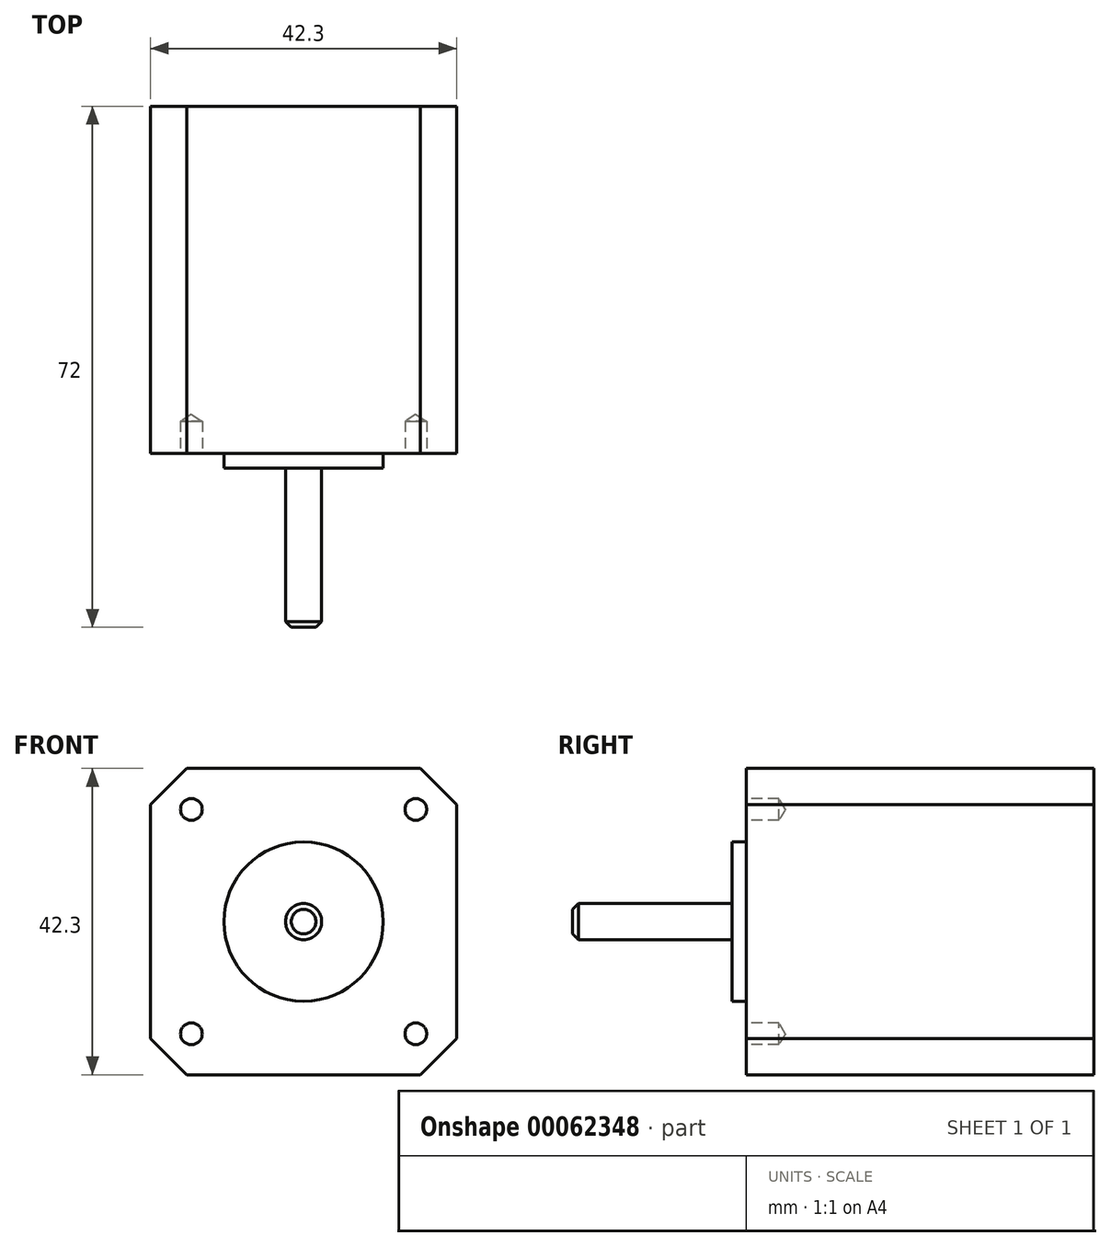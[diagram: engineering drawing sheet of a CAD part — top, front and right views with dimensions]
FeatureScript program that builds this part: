
annotation { "Feature Type Name" : "Feature", "Feature Type Description" : "" }
export const myFeature = defineFeature(function(context is Context, id is Id, definition is map)
    precondition{}
    {
        {
            var Q0;
            Q0=qCreatedBy(makeId("Front.planeOp"),FACE);
            var sketch = newSketch(context, id + "F0", { "sketchPlane" : qUnion([Q0])});
            skLineSegment(sketch, "E0.rect.bottom", {"start": v(21.15, -21.15) * mm, "end": v(-21.15, -21.15) * mm, "construction": true});
            skLineSegment(sketch, "E0.rect.top", {"start": v(21.15, 21.15) * mm, "end": v(-21.15, 21.15) * mm, "construction": true});
            skLineSegment(sketch, "E0.rect.left", {"start": v(21.15, -21.15) * mm, "end": v(21.15, 21.15) * mm, "construction": true});
            skLineSegment(sketch, "E0.rect.right", {"start": v(-21.15, -21.15) * mm, "end": v(-21.15, 21.15) * mm, "construction": true});
            skPoint(sketch, "E0.rect.middle", {"position": v(0, 0) * mm});
            skLineSegment(sketch, "E1", {"start": v(-16.15, 21.15) * mm, "end": v(-21.15, 16.15) * mm});
            skLineSegment(sketch, "E2", {"start": v(-21.15, -16.15) * mm, "end": v(-16.15, -21.15) * mm});
            skLineSegment(sketch, "E3", {"start": v(16.15, -21.15) * mm, "end": v(21.15, -16.15) * mm});
            skLineSegment(sketch, "E4", {"start": v(21.15, 16.15) * mm, "end": v(16.15, 21.15) * mm});
            skLineSegment(sketch, "E5", {"start": v(-16.15, 21.15) * mm, "end": v(16.15, 21.15) * mm});
            skLineSegment(sketch, "E6", {"start": v(21.15, 16.15) * mm, "end": v(21.15, -16.15) * mm});
            skLineSegment(sketch, "E7", {"start": v(16.15, -21.15) * mm, "end": v(-16.15, -21.15) * mm});
            skLineSegment(sketch, "E8", {"start": v(-21.15, -16.15) * mm, "end": v(-21.15, 16.15) * mm});
            skSolve(sketch);
        }
        {
            var Q0;
            Q0=makeQuery(id+"F0.imprint","IMPRINT",FACE,{"disambiguationData":[TD([[makeQuery(id+"F0.imprint","IMPRINT",EDGE,{"derivedFrom":sQuery(id+"F0.wireOp",EDGE,"E1")}),1.0]])]});
            extrude(context, id + "F1", {"entities" : qUnion([Q0]), "oppositeDirection" : true, "depth" : 48 * mm});
        }
        {
            var Q0;
            Q0=qCreatedBy(makeId("Right.planeOp"),FACE);
            var sketch = newSketch(context, id + "F2", { "sketchPlane" : qUnion([Q0])});
            skLineSegment(sketch, "E9", {"start": v(0, 0) * mm, "end": v(0, 11) * mm});
            skLineSegment(sketch, "E10", {"start": v(0, 11) * mm, "end": v(-2, 11) * mm});
            skLineSegment(sketch, "E11", {"start": v(-2, 11) * mm, "end": v(-2, 2.5) * mm});
            skLineSegment(sketch, "E12", {"start": v(-2, 2.5) * mm, "end": v(-23.2, 2.5) * mm});
            skLineSegment(sketch, "E13", {"start": v(-23.2, 2.5) * mm, "end": v(-24, 1.7) * mm});
            skLineSegment(sketch, "E14", {"start": v(-24, 1.7) * mm, "end": v(-24, 0) * mm});
            skLineSegment(sketch, "E15", {"start": v(-24, 0) * mm, "end": v(0, 0) * mm});
            skSolve(sketch);
        }
        {
            var Q0;
            Q0=makeQuery(id+"F2.imprint","IMPRINT",FACE,{"disambiguationData":[TD([[makeQuery(id+"F2.imprint","IMPRINT",EDGE,{"derivedFrom":sQuery(id+"F2.wireOp",EDGE,"E9")}),1.0]])]});
            var Q1;
            Q1=sQuery(id+"F2.wireOp",EDGE,"E15");
            revolve(context, id + "F3", {"operationType" : NewBodyOperationType.ADD, "entities" : qUnion([Q0]), "axis" : qUnion([Q1]), "revolveType" : RevolveType.FULL});
        }
        {
            var Q0;
            Q0=makeQuery(id+"F1.opExtrude","CAP_FACE",FACE,{"disambiguationData":[OSD([sQuery(id+"F0.wireOp",EDGE,"E1"),sQuery(id+"F0.wireOp",EDGE,"E2"),sQuery(id+"F0.wireOp",EDGE,"E3"),sQuery(id+"F0.wireOp",EDGE,"E4"),sQuery(id+"F0.wireOp",EDGE,"E5"),sQuery(id+"F0.wireOp",EDGE,"E6"),sQuery(id+"F0.wireOp",EDGE,"E7"),sQuery(id+"F0.wireOp",EDGE,"E8")])],"isStart":true});
            var sketch = newSketch(context, id + "F4", { "sketchPlane" : qUnion([Q0])});
            skPoint(sketch, "E16", {"position": v(-15.5, 15.5) * mm});
            skPoint(sketch, "E17", {"position": v(15.5, 15.5) * mm});
            skPoint(sketch, "E18", {"position": v(15.5, -15.5) * mm});
            skPoint(sketch, "E19", {"position": v(-15.5, -15.5) * mm});
            skSolve(sketch);
        }
        {
            var Q0;
            Q0=sQuery(id+"F4.wireOp",VERTEX,"E16");
            var Q1;
            Q1=sQuery(id+"F4.wireOp",VERTEX,"E17");
            var Q2;
            Q2=sQuery(id+"F4.wireOp",VERTEX,"E19");
            var Q3;
            Q3=sQuery(id+"F4.wireOp",VERTEX,"E18");
            var Q4;
            Q4=makeQuery(id+"F1.opExtrude","SWEPT_BODY",BODY,{"disambiguationData":[OSD([sQuery(id+"F0.wireOp",EDGE,"E1"),sQuery(id+"F0.wireOp",EDGE,"E2"),sQuery(id+"F0.wireOp",EDGE,"E3"),sQuery(id+"F0.wireOp",EDGE,"E4"),sQuery(id+"F0.wireOp",EDGE,"E5"),sQuery(id+"F0.wireOp",EDGE,"E6"),sQuery(id+"F0.wireOp",EDGE,"E7"),sQuery(id+"F0.wireOp",EDGE,"E8")])]});
            hole(context, id + "F5", {"style" : HoleStyle.SIMPLE, "holeDiameter" : 3 * mm, "endStyle" : HoleEndStyle.BLIND, "holeDepth" : 4.5 * mm, "locations" : qUnion([Q0, Q1, Q2, Q3]), "scope" : qUnion([Q4])});
        }
    });
